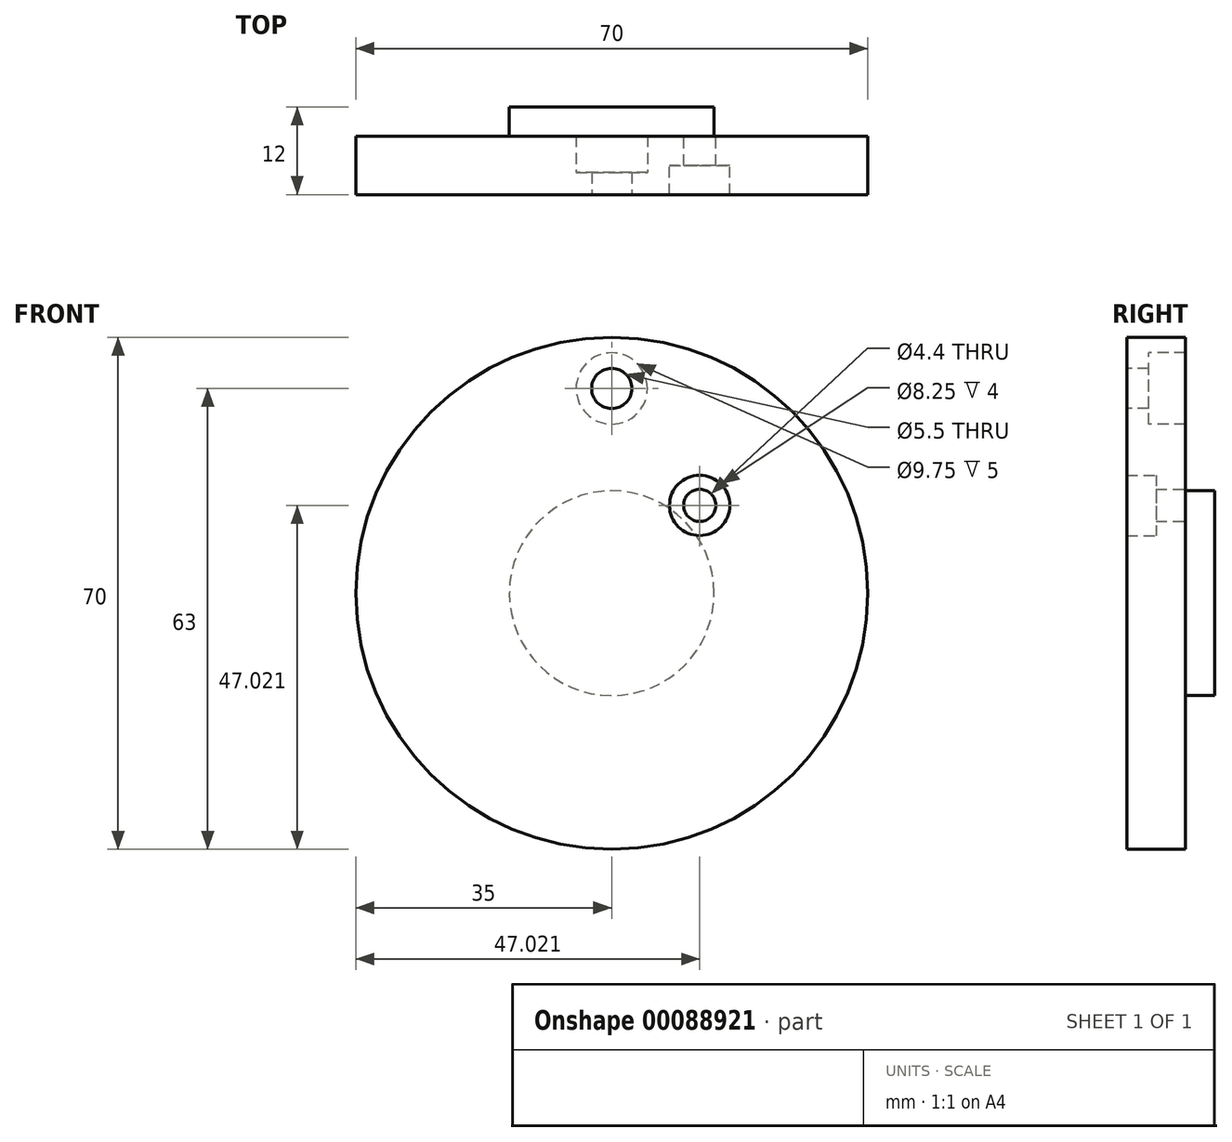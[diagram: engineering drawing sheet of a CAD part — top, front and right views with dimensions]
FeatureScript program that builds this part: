
annotation { "Feature Type Name" : "Feature", "Feature Type Description" : "" }
export const myFeature = defineFeature(function(context is Context, id is Id, definition is map)
    precondition{}
    {
        {
            var Q0;
            Q0=qCreatedBy(makeId("Front.planeOp"),FACE);
            var sketch = newSketch(context, id + "F0", { "sketchPlane" : qUnion([Q0])});
            skCircle(sketch, "E0", {"center": v(0, 0) * mm, "radius": 17 * mm, "construction": true});
            skCircle(sketch, "E1", {"center": v(0, 0) * mm, "radius": 28 * mm, "construction": true});
            skCircle(sketch, "E2", {"center": v(0, 0) * mm, "radius": 14 * mm});
            skCircle(sketch, "E3", {"center": v(0, 0) * mm, "radius": 35 * mm});
            skLineSegment(sketch, "E4", {"start": v(0, 0) * mm, "end": v(12.02, 12.02) * mm, "construction": true});
            skPoint(sketch, "E5", {"position": v(0, 28) * mm});
            skCircle(sketch, "E6", {"center": v(12.02, 12.02) * mm, "radius": 4.12 * mm, "construction": true});
            skCircle(sketch, "E7", {"center": v(0, 28) * mm, "radius": 4.88 * mm, "construction": true});
            skSolve(sketch);
        }
        {
            var Q0;
            Q0=makeQuery(id+"F0.imprint","IMPRINT",FACE,{"disambiguationData":[TD([[makeQuery(id+"F0.imprint","IMPRINT",EDGE,{"derivedFrom":sQuery(id+"F0.wireOp",EDGE,"E2")}),-1.0]])]});
            var Q1;
            Q1=makeQuery(id+"F0.imprint","IMPRINT",FACE,{"disambiguationData":[TD([[makeQuery(id+"F0.imprint","IMPRINT",EDGE,{"derivedFrom":sQuery(id+"F0.wireOp",EDGE,"E2")}),1.0]])]});
            extrude(context, id + "F1", {"entities" : qUnion([Q0, Q1]), "depth" : 8 * mm});
        }
        {
            var Q0;
            Q0=makeQuery(id+"F0.imprint","IMPRINT",FACE,{"disambiguationData":[TD([[makeQuery(id+"F0.imprint","IMPRINT",EDGE,{"derivedFrom":sQuery(id+"F0.wireOp",EDGE,"E2")}),1.0]])]});
            extrude(context, id + "F2", {"entities" : qUnion([Q0]), "operationType" : NewBodyOperationType.ADD, "oppositeDirection" : true, "depth" : 4 * mm});
        }
        {
            var Q0;
            Q0=makeQuery(id+"F1.opExtrude","CAP_FACE",FACE,{"disambiguationData":[OSD([sQuery(id+"F0.wireOp",EDGE,"E3")])],"isStart":false});
            var sketch = newSketch(context, id + "F3", { "sketchPlane" : qUnion([Q0])});
            skPoint(sketch, "E8.0", {"position": v(12.02, 12.02) * mm});
            skSolve(sketch);
        }
        {
            var Q0;
            Q0=sQuery(id+"F3.wireOp",VERTEX,"E8.0");
            var Q1;
            Q1=makeQuery(id+"F1.opExtrude","SWEPT_BODY",BODY,{"disambiguationData":[OSD([sQuery(id+"F0.wireOp",EDGE,"E3")])]});
            hole(context, id + "F4", {"style" : HoleStyle.C_BORE, "endStyle" : HoleEndStyle.THROUGH, "standardTappedOrClearance" : lookupTablePath({ "standard" : "ISO", "fit" : "Normal", "size" : "M4", "type" : "Clearance" }), "standardBlindInLast" : lookupTablePath({ "fit" : "Standard", "standard" : "ISO", "size" : "M4", "type" : "Clearance" }), "holeDiameter" : 4.4 * mm, "cBoreDiameter" : 8.25 * mm, "cBoreDepth" : 4 * mm, "locations" : qUnion([Q0]), "scope" : qUnion([Q1]), "isTappedThrough" : true, "startStyle" : HoleStartStyle.PART});
        }
        {
            var Q0;
            Q0=sQuery(id+"F0.wireOp",VERTEX,"E5");
            var Q1;
            Q1=makeQuery(id+"F1.opExtrude","SWEPT_BODY",BODY,{"disambiguationData":[OSD([sQuery(id+"F0.wireOp",EDGE,"E3")])]});
            hole(context, id + "F5", {"style" : HoleStyle.C_BORE, "endStyle" : HoleEndStyle.THROUGH, "oppositeDirection" : true, "standardTappedOrClearance" : lookupTablePath({ "standard" : "ISO", "fit" : "Normal", "size" : "M5", "type" : "Clearance" }), "standardBlindInLast" : lookupTablePath({ "fit" : "Standard", "standard" : "ISO", "size" : "M5", "type" : "Clearance" }), "holeDiameter" : 5.5 * mm, "cBoreDiameter" : 9.75 * mm, "cBoreDepth" : 5 * mm, "locations" : qUnion([Q0]), "scope" : qUnion([Q1]), "isTappedThrough" : true, "startStyle" : HoleStartStyle.PART});
        }
    });
